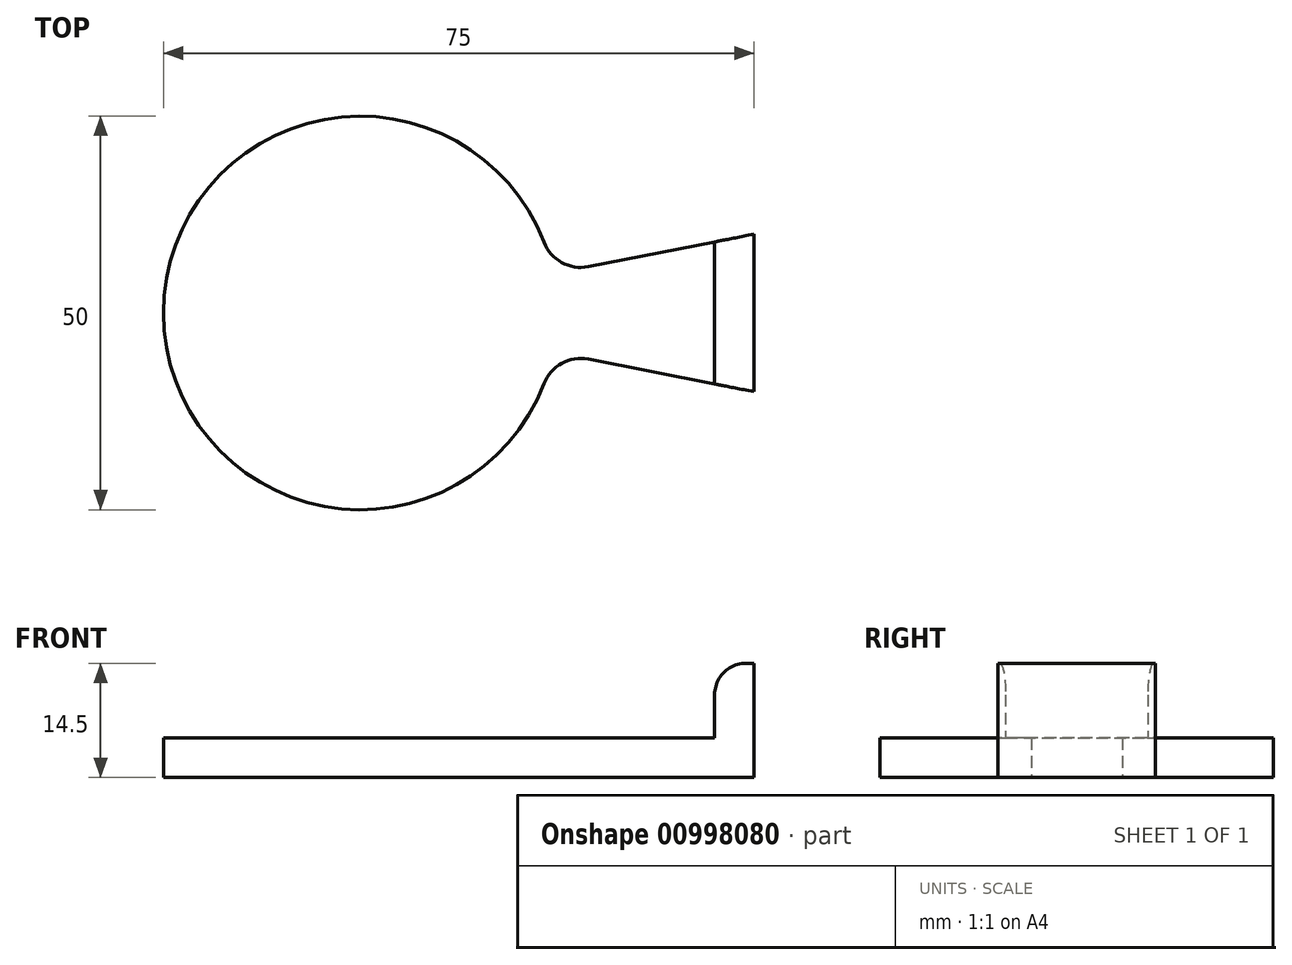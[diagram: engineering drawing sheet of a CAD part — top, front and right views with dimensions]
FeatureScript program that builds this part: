
annotation { "Feature Type Name" : "Feature", "Feature Type Description" : "" }
export const myFeature = defineFeature(function(context is Context, id is Id, definition is map)
    precondition{}
    {
        {
            var Q0;
            Q0=qCreatedBy(makeId("Top.planeOp"),FACE);
            var sketch = newSketch(context, id + "F0", { "sketchPlane" : qUnion([Q0])});
            skArc(sketch, "E0", {"start": v(24.5, 5) * mm, "mid": v(-25, 0) * mm, "end": v(24.5, -5) * mm});
            skLineSegment(sketch, "E1", {"start": v(50, 10) * mm, "end": v(50, -10) * mm});
            skLineSegment(sketch, "E2", {"start": v(50, 10) * mm, "end": v(24.5, 5) * mm});
            skLineSegment(sketch, "E3", {"start": v(50, -10) * mm, "end": v(24.5, -5) * mm});
            skSolve(sketch);
        }
        {
            var Q0;
            Q0 = qSketchRegion(id + "F0", true);
            extrude(context, id + "F1", {"entities" : qUnion([Q0]), "depth" : 5 * mm, "offsetDistance" : 25 * mm});
        }
        {
            var Q0;
            Q0=makeQuery(id+"F1.opExtrude","CAP_FACE",FACE,{"disambiguationData":[OSD([sQuery(id+"F0.wireOp",EDGE,"E0"),sQuery(id+"F0.wireOp",EDGE,"OeLScv3Z-fSen-120U-m1uw-jz7ILFs6pGsV"),sQuery(id+"F0.wireOp",EDGE,"E1"),sQuery(id+"F0.wireOp",EDGE,"PW4oO6fJ-s79T-s8FP-8qj6-iDoT8aQUYcft")])],"isStart":false});
            var sketch = newSketch(context, id + "F2", { "sketchPlane" : qUnion([Q0])});
            skLineSegment(sketch, "E4", {"start": v(50, 10) * mm, "end": v(50, -10) * mm});
            skLineSegment(sketch, "E5", {"start": v(50, -10) * mm, "end": v(45, -9.02) * mm});
            skLineSegment(sketch, "E6", {"start": v(45, -9.02) * mm, "end": v(45, 9.02) * mm});
            skLineSegment(sketch, "E7", {"start": v(45, 9.02) * mm, "end": v(50, 10) * mm});
            skSolve(sketch);
        }
        {
            var Q0;
            Q0 = qSketchRegion(id + "F2", true);
            extrude(context, id + "F3", {"entities" : qUnion([Q0]), "operationType" : NewBodyOperationType.ADD, "depth" : 9.5 * mm, "offsetDistance" : 25 * mm});
        }
        {
            var Q0;
            Q0=makeQuery(id+"F3.opExtrude","CAP_EDGE",EDGE,{"disambiguationData":[OSD([sQuery(id+"F2.wireOp",EDGE,"9oNVhxjQ-8aVT-r8zG-5EdK-15jCkIsodE6j.right")])],"isStart":true});
            var Q1;
            Q1=makeQuery(id+"F1.opExtrude","SWEPT_EDGE",EDGE,{"disambiguationData":[OSD([sQuery(id+"F0.wireOp",EDGE,"E0"),sQuery(id+"F0.wireOp",EDGE,"PW4oO6fJ-s79T-s8FP-8qj6-iDoT8aQUYcft")])]});
            var Q2;
            Q2=makeQuery(id+"F1.opExtrude","SWEPT_EDGE",EDGE,{"disambiguationData":[OSD([sQuery(id+"F0.wireOp",EDGE,"E0"),sQuery(id+"F0.wireOp",EDGE,"OeLScv3Z-fSen-120U-m1uw-jz7ILFs6pGsV")])]});
            var Q3;
            Q3=makeQuery(id+"F3.opExtrude","CAP_EDGE",EDGE,{"disambiguationData":[OSD([sQuery(id+"F2.wireOp",EDGE,"E6")])],"isStart":true});
            fillet(context, id + "F4", {"entities" : qUnion([Q0, Q1, Q2, Q3]), "radius" : 5 * mm, "tangentPropagation" : true, "allowEdgeOverflow" : false});
        }
        {
            var Q0;
            Q0=makeQuery(id+"F3.opExtrude","CAP_EDGE",EDGE,{"disambiguationData":[OSD([sQuery(id+"F2.wireOp",EDGE,"E6")])],"isStart":false});
            fillet(context, id + "F5", {"entities" : qUnion([Q0]), "radius" : 4 * mm, "tangentPropagation" : true, "allowEdgeOverflow" : false});
        }
    });
